# Revit family: Kessel AG 44700.20M en
name_source: partatom
category: Rohrzubehör
revit_build: Autodesk Revit 2014 (Build: 20130308_1515(x64)
units: mm (PartAtom-declared; Revit-internal decimal feet)

## types (1)
- Kessel AG 44700.20M en
    <1.010.00.2> Number of the part of the guideline = 38
    <1.010.00.3> Issue date (month) of the guideline = 201805
    <1.010.00.4> Manufacturer name = Kessel AG
    <1.010.00.5> Revision date of the file = Kessel AG
    <1.800.00.3> BS number = 00103200000200100000100000100300000000400100000008???00001
    <1.800.00.4> Comment field = Bodenablauf Der Ultraflache 79 DN 50, Klipsflansch, Schlitzrost
    <1.810.00.3> Manufacturer’s reference number = 44700.20M
    <1.810.00.4> DATANORM number = 44700.20M
    <38.100.00.4> Drain type for floor, roof and sanitary objects = Bodenabläufe mit Geruchsverschluss
    <38.110.00.4> Floor, roof and sanitary works sequences = Bodenablauf Der Ultraflache 79
    <38.200.00.3> Drain socket variation = waagerecht
    <38.250.00.3> Drainage type = Freispiegel
    <38.300.00.3> Type of drains for floor, roof and roofing objects = Ablauf-Punktförmig
    <38.360.00.3> Trace heating of the drain for floor, roof and sanitary objects = ohne Begleitheizung
    <38.400.00.3> Material of the drain body = Kunststoff
    <38.500.00.3> Sealing variantion = mit werksseitig angebrachter Manschette
    <38.550.00.3> Trap = mit Geruchverschluss
    <38.700.00.4> product name = Bodenablauf Der Ultraflache 79 DN 50, Klipsflansch, Schlitzrost
    <38.700.00.5> Temparturklasse = The Ultraflat 79 floor drain, DN 50, clipped flange, slotted cover
    <38.710.01.3> Product name = Bodenablauf Der Ultraflache 79 DN 50, Klipsflansch, Schlitzrost
    <38.710.01.4> Type = The Ultraflat 79 floor drain, DN 50, clipped flange, slotted cover
    CONNECTOR0_ref_dZ = 1 mm  [stored 0.00328084 ft]
    CONNECTOR1_DIAMETER_dNBN0_0r = 0 mm  [stored 0 ft]
    CONNECTOR1_dNBN0_00 = 127 mm
    CONNECTOR1_dNBN0_01 = 147 mm
    CONNECTOR1_ref_dNBN0 = 127 mm
    CONNECTOR1_ref_dNBN1 = 66 mm
    Hersteller = Kessel AG
    Modell = 44700.20M

note: [stored X ft] marks values corroborated as IEEE doubles in the binary element streams (Revit-internal decimal feet)
